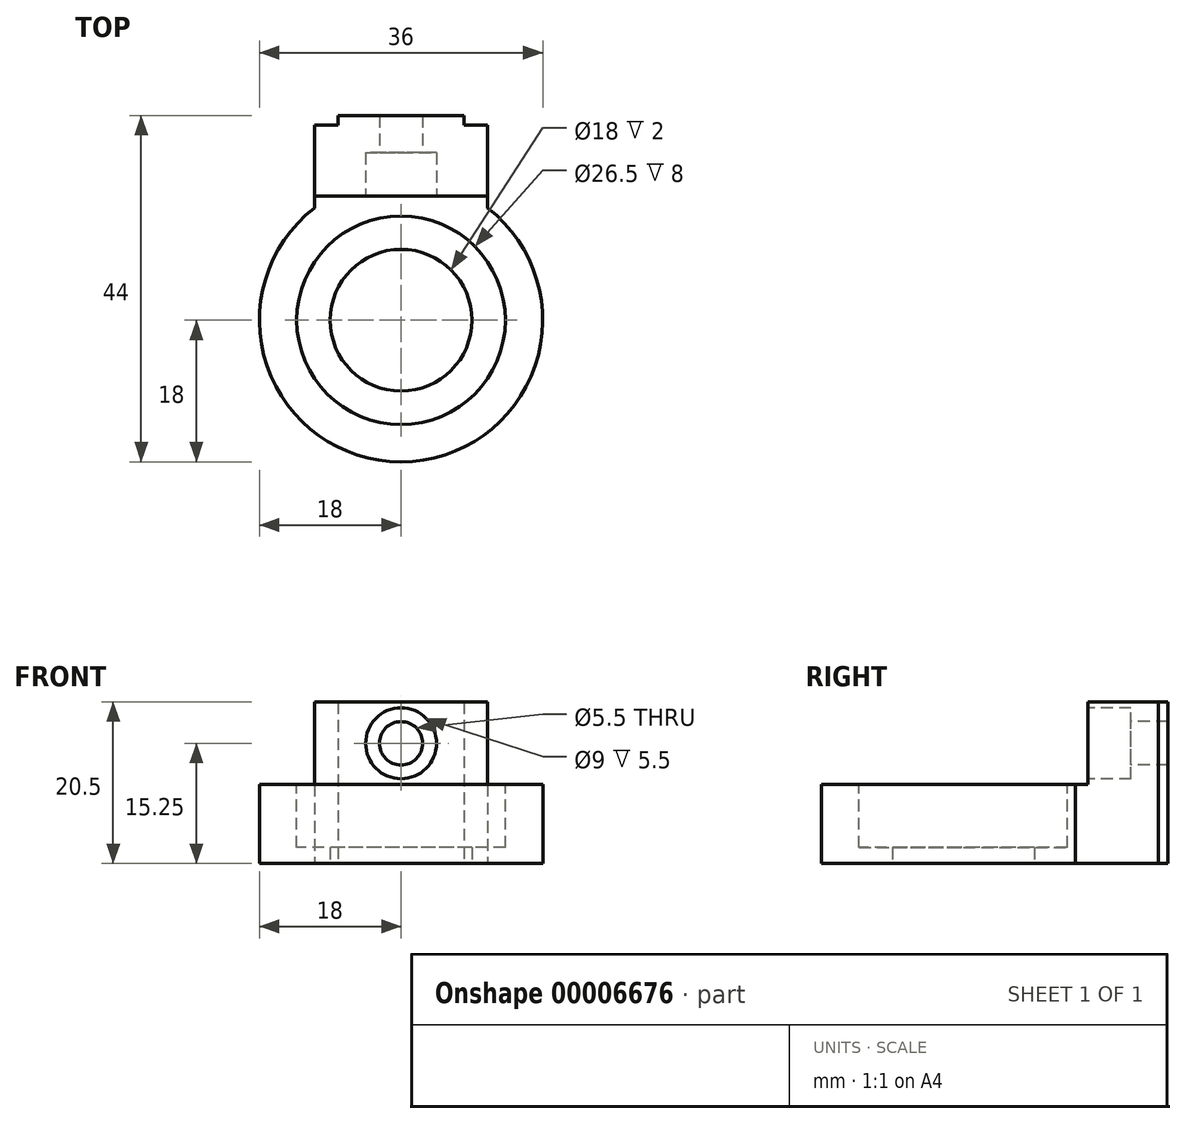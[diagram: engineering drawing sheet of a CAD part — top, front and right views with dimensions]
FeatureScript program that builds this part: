
annotation { "Feature Type Name" : "Feature", "Feature Type Description" : "" }
export const myFeature = defineFeature(function(context is Context, id is Id, definition is map)
    precondition{}
    {
        {
            var Q0;
            Q0=qCreatedBy(makeId("Top.planeOp"),FACE);
            var sketch = newSketch(context, id + "F0", { "sketchPlane" : qUnion([Q0])});
            skArc(sketch, "E0", {"start": v(-11, 14.25) * mm, "mid": v(0, -18) * mm, "end": v(11, 14.25) * mm});
            skCircle(sketch, "E1", {"center": v(0, 0) * mm, "radius": 9 * mm});
            skLineSegment(sketch, "E2.0", {"start": v(-11, 14.25) * mm, "end": v(-11, 24.8) * mm});
            skLineSegment(sketch, "E3.0", {"start": v(11, 14.25) * mm, "end": v(11, 24.8) * mm});
            skLineSegment(sketch, "E4.0", {"start": v(-8, 26) * mm, "end": v(8, 26) * mm});
            skLineSegment(sketch, "E5.0", {"start": v(-11, 24.8) * mm, "end": v(-8, 24.8) * mm});
            skLineSegment(sketch, "E6.trimOffspring", {"start": v(8, 24.8) * mm, "end": v(8, 26) * mm});
            skLineSegment(sketch, "E7.trimOffspring", {"start": v(-8, 24.8) * mm, "end": v(-8, 26) * mm});
            skLineSegment(sketch, "E8.trimOffspring", {"start": v(8, 24.8) * mm, "end": v(11, 24.8) * mm});
            skSolve(sketch);
        }
        {
            var Q0;
            Q0 = qSketchRegion(id + "F0", true);
            extrude(context, id + "F1", {"entities" : qUnion([Q0]), "depth" : 10 * mm});
        }
        {
            var Q0;
            Q0=makeQuery(id+"F1.opExtrude","CAP_FACE",FACE,{"disambiguationData":[OSD([sQuery(id+"F0.wireOp",EDGE,"E0"),sQuery(id+"F0.wireOp",EDGE,"E1"),sQuery(id+"F0.wireOp",EDGE,"E2.0"),sQuery(id+"F0.wireOp",EDGE,"E3.0"),sQuery(id+"F0.wireOp",EDGE,"E4.0"),sQuery(id+"F0.wireOp",EDGE,"E5.0"),sQuery(id+"F0.wireOp",EDGE,"E6.trimOffspring"),sQuery(id+"F0.wireOp",EDGE,"E7.trimOffspring"),sQuery(id+"F0.wireOp",EDGE,"E8.trimOffspring")])],"isStart":false});
            var sketch = newSketch(context, id + "F2", { "sketchPlane" : qUnion([Q0])});
            skCircle(sketch, "E9", {"center": v(0, 0) * mm, "radius": 13.25 * mm});
            skSolve(sketch);
        }
        {
            var Q0;
            Q0 = qSketchRegion(id + "F2", true);
            extrude(context, id + "F3", {"entities" : qUnion([Q0]), "operationType" : NewBodyOperationType.REMOVE, "oppositeDirection" : true, "depth" : 8 * mm});
        }
        {
            var Q0;
            Q0=makeQuery(id+"F1.opExtrude","CAP_FACE",FACE,{"disambiguationData":[OSD([sQuery(id+"F0.wireOp",EDGE,"E0"),sQuery(id+"F0.wireOp",EDGE,"E1"),sQuery(id+"F0.wireOp",EDGE,"E2.0"),sQuery(id+"F0.wireOp",EDGE,"E3.0"),sQuery(id+"F0.wireOp",EDGE,"E4.0"),sQuery(id+"F0.wireOp",EDGE,"E5.0"),sQuery(id+"F0.wireOp",EDGE,"E6.trimOffspring"),sQuery(id+"F0.wireOp",EDGE,"E7.trimOffspring"),sQuery(id+"F0.wireOp",EDGE,"E8.trimOffspring")])],"isStart":false});
            var sketch = newSketch(context, id + "F4", { "sketchPlane" : qUnion([Q0])});
            skLineSegment(sketch, "E10.bottom", {"start": v(-11, 24.8) * mm, "end": v(-8, 24.8) * mm});
            skLineSegment(sketch, "E10.top", {"start": v(-11, 15.8) * mm, "end": v(11, 15.8) * mm});
            skLineSegment(sketch, "E10.left", {"start": v(-11, 24.8) * mm, "end": v(-11, 15.8) * mm});
            skLineSegment(sketch, "E10.right", {"start": v(11, 24.8) * mm, "end": v(11, 15.8) * mm});
            skLineSegment(sketch, "E11.bottom", {"start": v(-8, 26) * mm, "end": v(8, 26) * mm});
            skLineSegment(sketch, "E11.left", {"start": v(-8, 26) * mm, "end": v(-8, 24.8) * mm});
            skLineSegment(sketch, "E11.right", {"start": v(8, 26) * mm, "end": v(8, 24.8) * mm});
            skLineSegment(sketch, "E12.trimOffspring", {"start": v(8, 24.8) * mm, "end": v(11, 24.8) * mm});
            skSolve(sketch);
        }
        {
            var Q0;
            Q0 = qSketchRegion(id + "F4", true);
            extrude(context, id + "F5", {"entities" : qUnion([Q0]), "operationType" : NewBodyOperationType.ADD, "depth" : 10.5 * mm});
        }
        {
            var Q0;
            Q0=makeQuery(id+"F5.opExtrude","SWEPT_FACE",FACE,{"disambiguationData":[OSD([sQuery(id+"F4.wireOp",EDGE,"E10.top")])]});
            var sketch = newSketch(context, id + "F6", { "sketchPlane" : qUnion([Q0])});
            skCircle(sketch, "E13", {"center": v(0, 15.25) * mm, "radius": 2.75 * mm});
            skSolve(sketch);
        }
        {
            var Q0;
            Q0 = qSketchRegion(id + "F6", true);
            extrude(context, id + "F7", {"entities" : qUnion([Q0]), "operationType" : NewBodyOperationType.REMOVE, "endBound" : BoundingType.THROUGH_ALL, "oppositeDirection" : true, "depth" : 25 * mm});
        }
        {
            var Q0;
            Q0=makeQuery(id+"F5.opExtrude","SWEPT_FACE",FACE,{"disambiguationData":[OSD([sQuery(id+"F4.wireOp",EDGE,"E10.top")])]});
            var sketch = newSketch(context, id + "F8", { "sketchPlane" : qUnion([Q0])});
            skCircle(sketch, "E14", {"center": v(0, 15.25) * mm, "radius": 4.5 * mm});
            skSolve(sketch);
        }
        {
            var Q0;
            Q0 = qSketchRegion(id + "F8", true);
            extrude(context, id + "F9", {"entities" : qUnion([Q0]), "operationType" : NewBodyOperationType.REMOVE, "oppositeDirection" : true, "depth" : 5.5 * mm});
        }
    });
